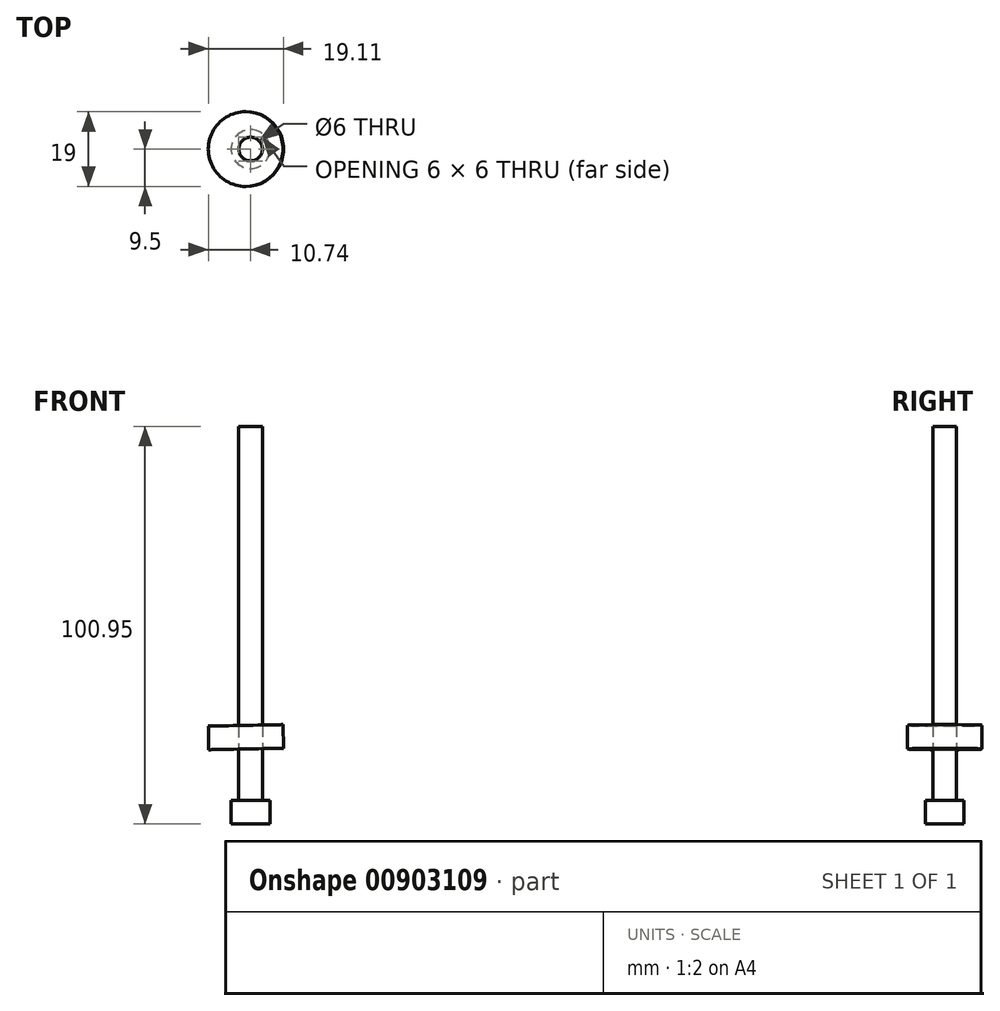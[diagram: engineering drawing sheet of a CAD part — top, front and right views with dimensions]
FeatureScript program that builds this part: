
annotation { "Feature Type Name" : "Feature", "Feature Type Description" : "" }
export const myFeature = defineFeature(function(context is Context, id is Id, definition is map)
    precondition{}
    {
        {
            var Q0;
            Q0=qCreatedBy(makeId("Top.planeOp"),FACE);
            var sketch = newSketch(context, id + "F0", { "sketchPlane" : qUnion([Q0])});
            skCircle(sketch, "E0", {"center": v(0, 0) * mm, "radius": 4.92 * mm});
            skSolve(sketch);
        }
        {
            var Q0;
            Q0 = qSketchRegion(id + "F0", true);
            extrude(context, id + "F1", {"entities" : qUnion([Q0]), "depth" : 5.95 * mm, "offsetDistance" : 25 * mm});
        }
        {
            var Q0;
            Q0=makeQuery(id+"F1.opExtrude","CAP_FACE",FACE,{"disambiguationData":[OSD([sQuery(id+"F0.wireOp",EDGE,"E0")])],"isStart":false});
            var sketch = newSketch(context, id + "F2", { "sketchPlane" : qUnion([Q0])});
            skCircle(sketch, "E1", {"center": v(0, 0) * mm, "radius": 3 * mm});
            skSolve(sketch);
        }
        {
            var Q0;
            Q0=makeQuery(id+"F2.imprint","IMPRINT",FACE,{"disambiguationData":[TD([[makeQuery(id+"F2.imprint","IMPRINT",EDGE,{"derivedFrom":sQuery(id+"F2.wireOp",EDGE,"E1")}),1.0]])]});
            extrude(context, id + "F3", {"entities" : qUnion([Q0]), "operationType" : NewBodyOperationType.ADD, "depth" : 95 * mm, "offsetDistance" : 25 * mm});
        }
        {
            var Q0;
            Q0=qCreatedBy(makeId("Front.planeOp"),FACE);
            var sketch = newSketch(context, id + "F4", { "sketchPlane" : qUnion([Q0])});
            skCircle(sketch, "E2", {"center": v(0, 19.06) * mm, "radius": 6.74 * mm});
            skSolve(sketch);
        }
        {
            var Q0;
            Q0=sQuery(id+"F4.wireOp",EDGE,"E2");
            cPlane(context, id + "F5", {"entities" : qUnion([Q0]), "cplaneType" : CPlaneType.LINE_ANGLE, "offset" : 25 * mm, "angle" : 1.15 * degree, "width" : 150 * mm, "height" : 150 * mm});
        }
        {
            var Q0;
            Q0=qCreatedBy(id+"F5.planeOp",FACE);
            var sketch = newSketch(context, id + "F6", { "sketchPlane" : qUnion([Q0])});
            skCircle(sketch, "E3", {"center": v(-0.75, 0) * mm, "radius": 9.5 * mm});
            skSolve(sketch);
        }
        {
            var Q0;
            Q0=makeQuery(id+"F6.imprint","IMPRINT",FACE,{"disambiguationData":[TD([[makeQuery(id+"F6.imprint","IMPRINT",EDGE,{"derivedFrom":sQuery(id+"F6.wireOp",EDGE,"E3")}),1.0]])]});
            extrude(context, id + "F7", {"entities" : qUnion([Q0]), "oppositeDirection" : true, "depth" : 6 * mm, "offsetDistance" : 25 * mm});
        }
        {
            var Q0;
            Q0=makeQuery(id+"F1.opExtrude","SWEPT_BODY",BODY,{"disambiguationData":[OSD([sQuery(id+"F0.wireOp",EDGE,"E0")])]});
            var Q1;
            Q1=makeQuery(id+"F7.opExtrude","SWEPT_BODY",BODY,{"disambiguationData":[OSD([sQuery(id+"F6.wireOp",EDGE,"E3")])]});
            booleanBodies(context, id + "F8", {"operationType" : BooleanOperationType.SUBTRACTION, "tools" : qUnion([Q0]), "targets" : qUnion([Q1]), "keepTools" : true});
        }
    });
